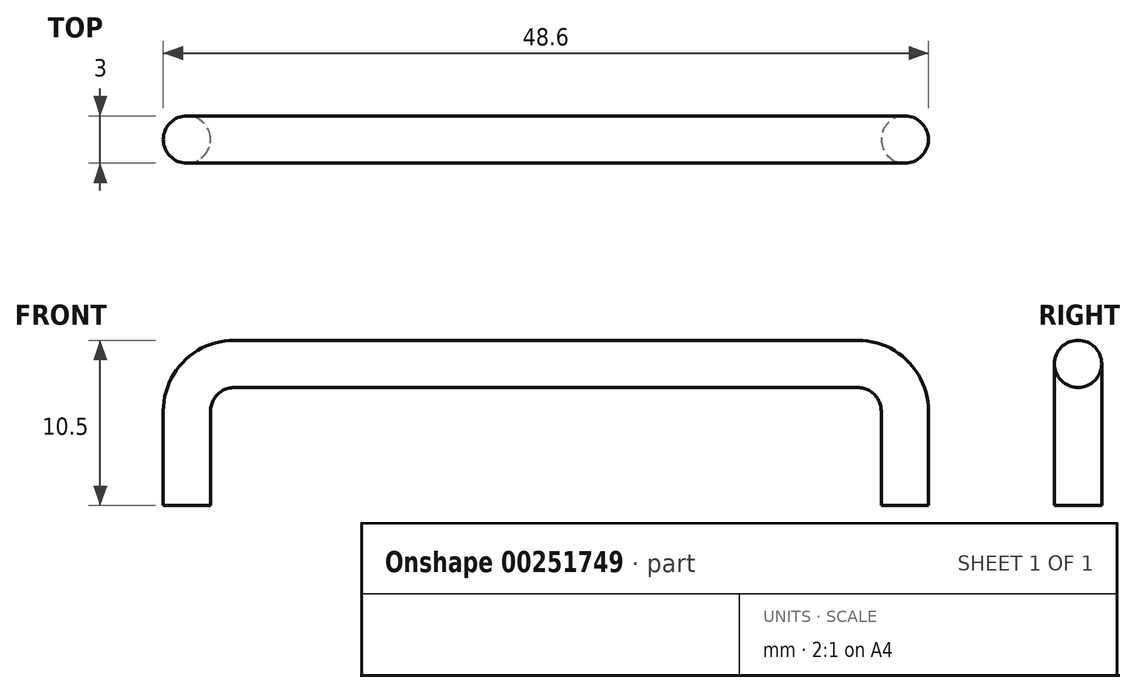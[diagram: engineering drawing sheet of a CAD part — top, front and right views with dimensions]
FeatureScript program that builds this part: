
annotation { "Feature Type Name" : "Feature", "Feature Type Description" : "" }
export const myFeature = defineFeature(function(context is Context, id is Id, definition is map)
    precondition{}
    {
        {
            var Q0;
            Q0=qCreatedBy(makeId("Front.planeOp"),FACE);
            var sketch = newSketch(context, id + "F0", { "sketchPlane" : qUnion([Q0])});
            skPoint(sketch, "E0.middle", {"position": v(0, 0) * mm});
            skLineSegment(sketch, "E1", {"start": v(-19.8, 0) * mm, "end": v(19.8, 0) * mm});
            skPoint(sketch, "E1.startSnap0", {"position": v(-24.3, 0) * mm});
            skPoint(sketch, "E1.endSnap0", {"position": v(24.3, 0) * mm});
            skLineSegment(sketch, "E2", {"start": v(-22.8, -9) * mm, "end": v(-22.8, -3) * mm});
            skLineSegment(sketch, "E3", {"start": v(22.8, -3) * mm, "end": v(22.8, -9) * mm});
            skPoint(sketch, "E4.orphan", {"position": v(-36.53, 0) * mm});
            skPoint(sketch, "E5.orphan", {"position": v(46.15, 0) * mm});
            skPoint(sketch, "E6.orphan", {"position": v(-24.3, -1.5) * mm});
            skPoint(sketch, "E7.trimOffspring.end.orphan", {"position": v(-24.3, 1.5) * mm});
            skPoint(sketch, "E8.orphan", {"position": v(24.3, 1.5) * mm});
            skPoint(sketch, "E0.left.start.orphan", {"position": v(24.3, -1.5) * mm});
            skPoint(sketch, "E9.visualSharp", {"position": v(-22.8, 0) * mm});
            skArc(sketch, "E9.filletArc", {"start": v(-19.8, 0) * mm, "mid": v(-21.92, -0.88) * mm, "end": v(-22.8, -3) * mm});
            skPoint(sketch, "E10.visualSharp", {"position": v(22.8, 0) * mm});
            skArc(sketch, "E10.filletArc", {"start": v(22.8, -3) * mm, "mid": v(21.92, -0.88) * mm, "end": v(19.8, 0) * mm});
            skSolve(sketch);
        }
        {
            var Q0;
            Q0=qCreatedBy(makeId("Top.planeOp"),FACE);
            cPlane(context, id + "F1", {"entities" : qUnion([Q0]), "cplaneType" : CPlaneType.OFFSET, "offset" : 9 * mm, "oppositeDirection" : true, "width" : 150 * mm, "height" : 150 * mm});
        }
        {
            var Q0;
            Q0=qCreatedBy(id+"F1.planeOp",FACE);
            var sketch = newSketch(context, id + "F2", { "sketchPlane" : qUnion([Q0])});
            skPoint(sketch, "E11.0", {"position": v(22.8, 0) * mm});
            skCircle(sketch, "E12", {"center": v(22.8, 0) * mm, "radius": 1.5 * mm});
            skSolve(sketch);
        }
        {
            var Q0;
            Q0=makeQuery(id+"F2.imprint","IMPRINT",FACE,{"disambiguationData":[TD([[makeQuery(id+"F2.imprint","IMPRINT",EDGE,{"derivedFrom":sQuery(id+"F2.wireOp",EDGE,"E12")}),1.0]])]});
            var Q1;
            Q1=sQuery(id+"F0.wireOp",EDGE,"E3");
            var Q2;
            Q2=sQuery(id+"F0.wireOp",EDGE,"E10.filletArc");
            var Q3;
            Q3=sQuery(id+"F0.wireOp",EDGE,"E1");
            var Q4;
            Q4=sQuery(id+"F0.wireOp",EDGE,"E9.filletArc");
            var Q5;
            Q5=sQuery(id+"F0.wireOp",EDGE,"E2");
            sweep(context, id + "F3", {"profiles" : qUnion([Q0]), "path" : qUnion([Q1, Q2, Q3, Q4, Q5])});
        }
    });
